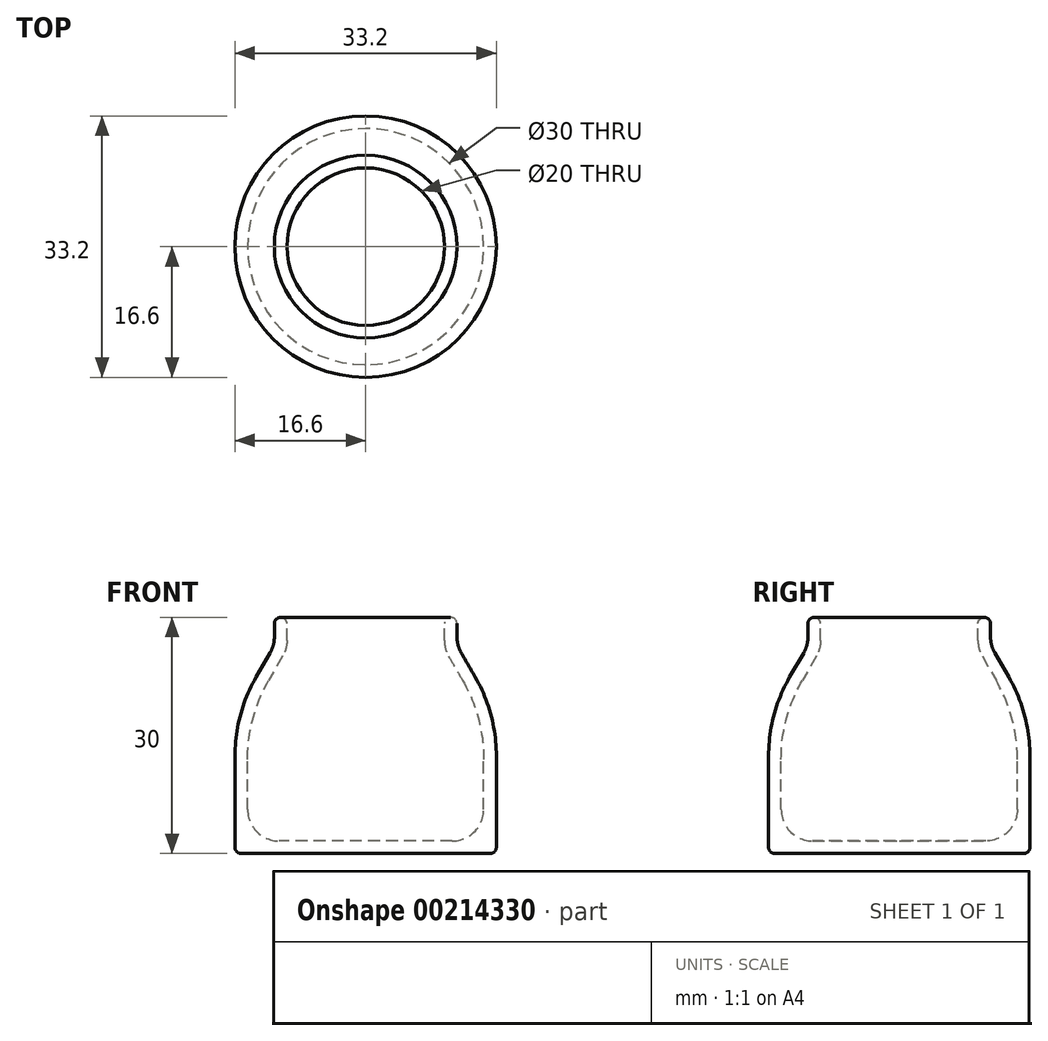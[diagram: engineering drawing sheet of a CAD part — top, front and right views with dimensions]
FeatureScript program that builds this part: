
annotation { "Feature Type Name" : "Feature", "Feature Type Description" : "" }
export const myFeature = defineFeature(function(context is Context, id is Id, definition is map)
    precondition{}
    {
        {
            var Q0;
            Q0=qCreatedBy(makeId("Front.planeOp"),FACE);
            var sketch = newSketch(context, id + "F0", { "sketchPlane" : qUnion([Q0])});
            skLineSegment(sketch, "E0", {"start": v(0, 0) * mm, "end": v(-15.8, 0) * mm});
            skLineSegment(sketch, "E1", {"start": v(-16.6, 0.8) * mm, "end": v(-16.6, 12.4) * mm});
            skLineSegment(sketch, "E2", {"start": v(-13.92, 22.4) * mm, "end": v(-12.14, 25.5) * mm});
            skLineSegment(sketch, "E3", {"start": v(-11.6, 27.5) * mm, "end": v(-11.6, 29.2) * mm});
            skLineSegment(sketch, "E4", {"start": v(-10.8, 30) * mm, "end": v(-10.8, 30) * mm});
            skLineSegment(sketch, "E5", {"start": v(-10, 29.2) * mm, "end": v(-10, 27.07) * mm});
            skLineSegment(sketch, "E6", {"start": v(-10.54, 25.07) * mm, "end": v(-12.32, 21.98) * mm});
            skLineSegment(sketch, "E7", {"start": v(-15, 11.98) * mm, "end": v(-15, 5.6) * mm});
            skLineSegment(sketch, "E8", {"start": v(0, 1.6) * mm, "end": v(0, 0) * mm});
            skPoint(sketch, "E9.visualSharp", {"position": v(-11.6, 30) * mm});
            skArc(sketch, "E9.filletArc", {"start": v(-10.8, 30) * mm, "mid": v(-11.37, 29.77) * mm, "end": v(-11.6, 29.2) * mm});
            skPoint(sketch, "E10.visualSharp", {"position": v(-10, 30) * mm});
            skArc(sketch, "E10.filletArc", {"start": v(-10, 29.2) * mm, "mid": v(-10.23, 29.77) * mm, "end": v(-10.8, 30) * mm});
            skPoint(sketch, "E11.visualSharp", {"position": v(-16.6, 0) * mm});
            skArc(sketch, "E11.filletArc", {"start": v(-16.6, 0.8) * mm, "mid": v(-16.37, 0.23) * mm, "end": v(-15.8, 0) * mm});
            skPoint(sketch, "E12.visualSharp", {"position": v(-16.6, 17.77) * mm});
            skArc(sketch, "E12.filletArc", {"start": v(-13.92, 22.4) * mm, "mid": v(-15.92, 17.59) * mm, "end": v(-16.6, 12.4) * mm});
            skPoint(sketch, "E13.visualSharp", {"position": v(-15, 17.34) * mm});
            skArc(sketch, "E13.filletArc", {"start": v(-12.32, 21.98) * mm, "mid": v(-14.32, 17.16) * mm, "end": v(-15, 11.98) * mm});
            skPoint(sketch, "E14.visualSharp", {"position": v(-10, 26) * mm});
            skArc(sketch, "E14.filletArc", {"start": v(-10.54, 25.07) * mm, "mid": v(-10.14, 26.04) * mm, "end": v(-10, 27.07) * mm});
            skPoint(sketch, "E15.visualSharp", {"position": v(-11.6, 26.43) * mm});
            skArc(sketch, "E15.filletArc", {"start": v(-12.14, 25.5) * mm, "mid": v(-11.74, 26.47) * mm, "end": v(-11.6, 27.5) * mm});
            skLineSegment(sketch, "E16", {"start": v(0, 42.5) * mm, "end": v(0, -7.04) * mm, "construction": true});
            skLineSegment(sketch, "E17", {"start": v(0, 1.6) * mm, "end": v(-11, 1.6) * mm});
            skPoint(sketch, "E18.visualSharp", {"position": v(-15, 1.6) * mm});
            skArc(sketch, "E18.filletArc", {"start": v(-15, 5.6) * mm, "mid": v(-13.83, 2.77) * mm, "end": v(-11, 1.6) * mm});
            skSolve(sketch);
        }
        {
            var Q0;
            Q0 = qSketchRegion(id + "F0", true);
            var Q1;
            Q1=sQuery(id+"F0.wireOp",EDGE,"E16");
            revolve(context, id + "F1", {"entities" : qUnion([Q0]), "axis" : qUnion([Q1]), "revolveType" : RevolveType.FULL});
        }
    });
